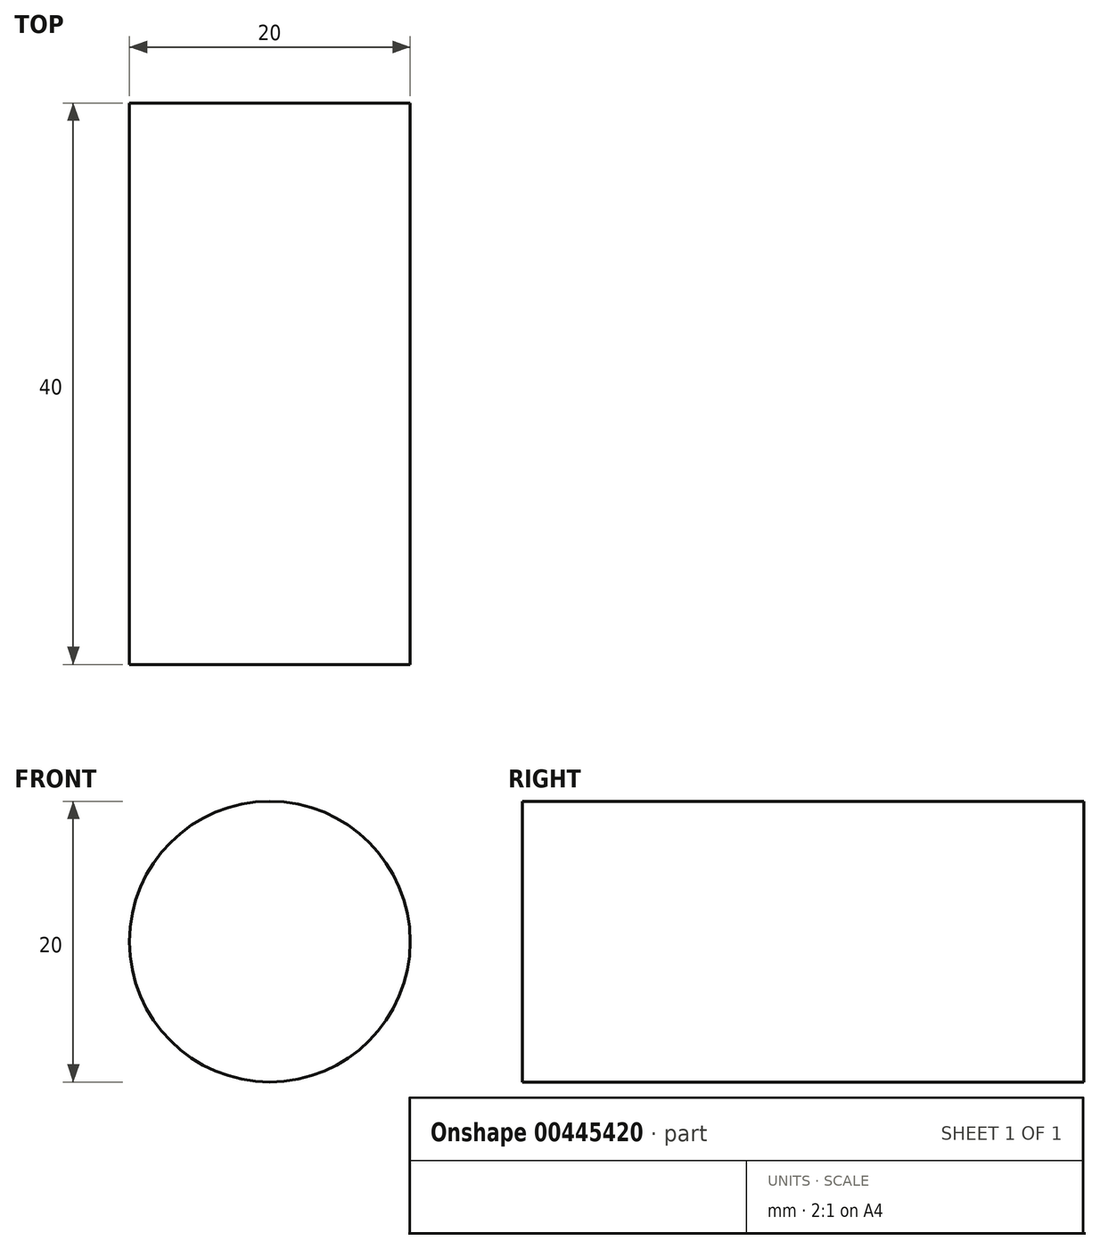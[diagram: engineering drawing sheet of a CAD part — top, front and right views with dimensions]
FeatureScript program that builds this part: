
annotation { "Feature Type Name" : "Feature", "Feature Type Description" : "" }
export const myFeature = defineFeature(function(context is Context, id is Id, definition is map)
    precondition{}
    {
        {
            var Q0;
            Q0=qCreatedBy(makeId("Front.planeOp"),FACE);
            var sketch = newSketch(context, id + "F0", { "sketchPlane" : qUnion([Q0])});
            skCircle(sketch, "E0", {"center": v(0, 0) * mm, "radius": 10 * mm});
            skSolve(sketch);
        }
        {
            var Q0;
            Q0=makeQuery(id+"F0.imprint","IMPRINT",FACE,{"disambiguationData":[TD([[makeQuery(id+"F0.imprint","IMPRINT",EDGE,{"derivedFrom":sQuery(id+"F0.wireOp",EDGE,"E0")}),1.0]])]});
            extrude(context, id + "F1", {"entities" : qUnion([Q0]), "depth" : 40 * mm});
        }
    });
